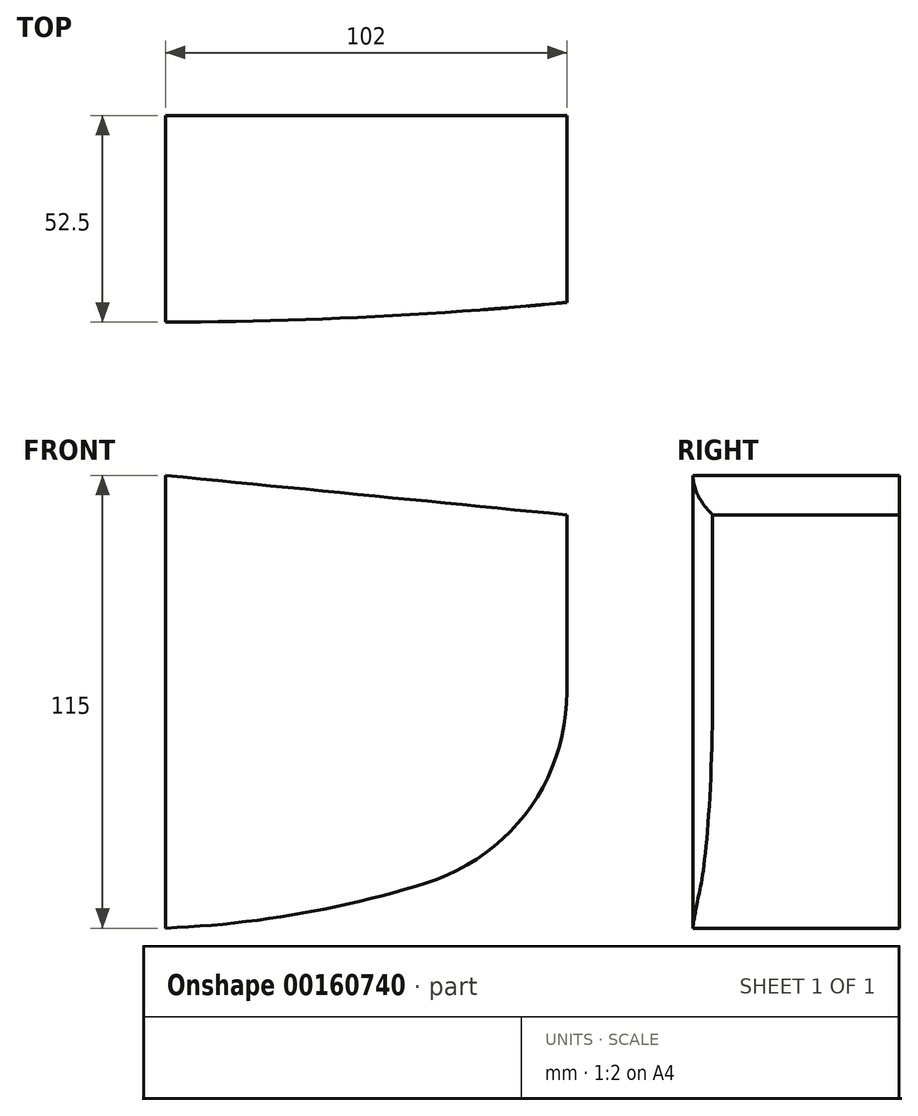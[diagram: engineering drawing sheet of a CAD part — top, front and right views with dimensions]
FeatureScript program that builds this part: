
annotation { "Feature Type Name" : "Feature", "Feature Type Description" : "" }
export const myFeature = defineFeature(function(context is Context, id is Id, definition is map)
    precondition{}
    {
        {
            var Q0;
            Q0=qCreatedBy(makeId("Front.planeOp"),FACE);
            var sketch = newSketch(context, id + "F0", { "sketchPlane" : qUnion([Q0])});
            skLineSegment(sketch, "E0", {"start": v(-102, 32.5) * mm, "end": v(-102, -82.5) * mm});
            skLineSegment(sketch, "E1", {"start": v(0, 22.5) * mm, "end": v(0, -22.5) * mm});
            skLineSegment(sketch, "E2", {"start": v(0, 22.5) * mm, "end": v(-102, 32.5) * mm});
            skArc(sketch, "E3", {"start": v(0, -22.5) * mm, "mid": v(-9.88, -52.6) * mm, "end": v(-35.66, -71) * mm});
            skArc(sketch, "E4", {"start": v(-102, -82.5) * mm, "mid": v(-68.45, -78.92) * mm, "end": v(-35.66, -71) * mm});
            skSolve(sketch);
        }
        {
            var Q0;
            Q0=qCreatedBy(makeId("Right.planeOp"),FACE);
            var sketch = newSketch(context, id + "F1", { "sketchPlane" : qUnion([Q0])});
            skCircle(sketch, "E5", {"center": v(0, 0) * mm, "radius": 20 * mm, "construction": true});
            skCircle(sketch, "E6", {"center": v(0, 0) * mm, "radius": 10 * mm, "construction": true});
            skArc(sketch, "E7", {"start": v(-21.81, 5.51) * mm, "mid": v(-22.33, 2.78) * mm, "end": v(-22.5, 0) * mm, "construction": true});
            skLineSegment(sketch, "E8", {"start": v(-23.75, 8) * mm, "end": v(-42.5, 8) * mm, "construction": true});
            skLineSegment(sketch, "E9", {"start": v(-44.5, 6) * mm, "end": v(-44.5, 0) * mm, "construction": true});
            skLineSegment(sketch, "E10", {"start": v(-22.37, 11) * mm, "end": v(-42.5, 11) * mm});
            skLineSegment(sketch, "E11", {"start": v(-47.5, 6) * mm, "end": v(-47.5, -2) * mm});
            skLineSegment(sketch, "E12", {"start": v(-42.5, -7) * mm, "end": v(-35, -7) * mm});
            skLineSegment(sketch, "E13", {"start": v(-10, -32) * mm, "end": v(-10, -47.27) * mm});
            skLineSegment(sketch, "E14", {"start": v(-24.5, -2) * mm, "end": v(-42.5, -2) * mm, "construction": true});
            skPoint(sketch, "E15.visualSharp", {"position": v(-10, -7) * mm});
            skArc(sketch, "E15.filletArc", {"start": v(-10, -32) * mm, "mid": v(-17.32, -14.32) * mm, "end": v(-35, -7) * mm});
            skLineSegment(sketch, "E16", {"start": v(0, 22.5) * mm, "end": v(0, -47.56) * mm});
            skLineSegment(sketch, "E17", {"start": v(0, -47.56) * mm, "end": v(-10, -47.27) * mm});
            skArc(sketch, "E18.trimOffspring", {"start": v(0, 22.5) * mm, "mid": v(-10.29, 20) * mm, "end": v(-18.3, 13.1) * mm});
            skPoint(sketch, "E19.visualSharp", {"position": v(-44.5, 8) * mm});
            skArc(sketch, "E19.filletArc", {"start": v(-42.5, 8) * mm, "mid": v(-43.91, 7.41) * mm, "end": v(-44.5, 6) * mm, "construction": true});
            skPoint(sketch, "E20.visualSharp", {"position": v(-21.03, 8) * mm});
            skArc(sketch, "E20.filletArc", {"start": v(-21.81, 5.51) * mm, "mid": v(-22.18, 7.23) * mm, "end": v(-23.75, 8) * mm, "construction": true});
            skPoint(sketch, "E21.visualSharp", {"position": v(-22.41, -2) * mm});
            skArc(sketch, "E21.filletArc", {"start": v(-24.5, -2) * mm, "mid": v(-23.09, -1.41) * mm, "end": v(-22.5, 0) * mm, "construction": true});
            skPoint(sketch, "E22.visualSharp", {"position": v(-44.5, -2) * mm});
            skArc(sketch, "E22.filletArc", {"start": v(-44.5, 0) * mm, "mid": v(-43.91, -1.41) * mm, "end": v(-42.5, -2) * mm, "construction": true});
            skPoint(sketch, "E23.visualSharp", {"position": v(-19.63, 11) * mm});
            skArc(sketch, "E23.filletArc", {"start": v(-22.37, 11) * mm, "mid": v(-20.08, 11.55) * mm, "end": v(-18.3, 13.1) * mm});
            skPoint(sketch, "E24.visualSharp", {"position": v(-47.5, 11) * mm});
            skArc(sketch, "E24.filletArc", {"start": v(-42.5, 11) * mm, "mid": v(-46.04, 9.54) * mm, "end": v(-47.5, 6) * mm});
            skPoint(sketch, "E25.visualSharp", {"position": v(-47.5, -7) * mm});
            skArc(sketch, "E25.filletArc", {"start": v(-47.5, -2) * mm, "mid": v(-46.04, -5.54) * mm, "end": v(-42.5, -7) * mm});
            skSolve(sketch);
        }
        {
            var Q0;
            Q0=qCreatedBy(makeId("Right.planeOp"),FACE);
            var Q1;
            Q1=sQuery(id+"F0.wireOp",VERTEX,"E0.start");
            cPlane(context, id + "F2", {"entities" : qUnion([Q0, Q1]), "cplaneType" : CPlaneType.PLANE_POINT, "offset" : 25 * mm, "width" : 150 * mm, "height" : 150 * mm});
        }
        {
            var Q0;
            Q0=qCreatedBy(id+"F2.planeOp",FACE);
            var sketch = newSketch(context, id + "F3", { "sketchPlane" : qUnion([Q0])});
            skPoint(sketch, "E26.0", {"position": v(0, 32.5) * mm});
            skPoint(sketch, "E27.0", {"position": v(0, -82.5) * mm});
            skLineSegment(sketch, "E28.0", {"start": v(0, 32.5) * mm, "end": v(0, -82.5) * mm});
            skArc(sketch, "E29", {"start": v(0, 32.5) * mm, "mid": v(-25.65, 28.28) * mm, "end": v(-48.59, 16.06) * mm});
            skLineSegment(sketch, "E30", {"start": v(-49.95, -44.45) * mm, "end": v(-52.5, 7.62) * mm});
            skArc(sketch, "E31", {"start": v(-52.5, 7.62) * mm, "mid": v(-51.58, 12.32) * mm, "end": v(-48.59, 16.06) * mm});
            skLineSegment(sketch, "E32", {"start": v(0, -82.5) * mm, "end": v(-10, -82.5) * mm});
            skArc(sketch, "E33", {"start": v(-10, -82.5) * mm, "mid": v(-37.58, -71.47) * mm, "end": v(-49.95, -44.45) * mm});
            skSolve(sketch);
        }
        {
            var Q0;
            Q0=qCreatedBy(makeId("Top.planeOp"),FACE);
            var sketch = newSketch(context, id + "F4", { "sketchPlane" : qUnion([Q0])});
            skPoint(sketch, "E34.0", {"position": v(-102, -52.5) * mm});
            skPoint(sketch, "E35.0", {"position": v(0, -47.5) * mm});
            skPoint(sketch, "E36.0", {"position": v(-102, 0) * mm});
            skLineSegment(sketch, "E37", {"start": v(-102, 0) * mm, "end": v(-102, -52.5) * mm});
            skArc(sketch, "E38", {"start": v(-102, -52.5) * mm, "mid": v(-50.94, -51.25) * mm, "end": v(0, -47.5) * mm});
            skLineSegment(sketch, "E39", {"start": v(0, 0) * mm, "end": v(0, -22.5) * mm});
            skLineSegment(sketch, "E40", {"start": v(0, 0) * mm, "end": v(-102, 0) * mm});
            skLineSegment(sketch, "E41", {"start": v(0, -47.5) * mm, "end": v(0, -22.5) * mm});
            skSolve(sketch);
        }
        {
            var Q0;
            Q0=makeQuery(id+"F0.imprint","IMPRINT",FACE,{"disambiguationData":[TD([[makeQuery(id+"F0.imprint","IMPRINT",EDGE,{"derivedFrom":sQuery(id+"F0.wireOp",EDGE,"E0")}),1.0]])]});
            extrude(context, id + "F5", {"entities" : qUnion([Q0]), "depth" : 65 * mm});
        }
        {
            var Q0;
            Q0 = qSketchRegion(id + "F4", true);
            extrude(context, id + "F6", {"entities" : qUnion([Q0]), "operationType" : NewBodyOperationType.INTERSECT, "endBound" : BoundingType.SYMMETRIC, "depth" : 200 * mm});
        }
    });
